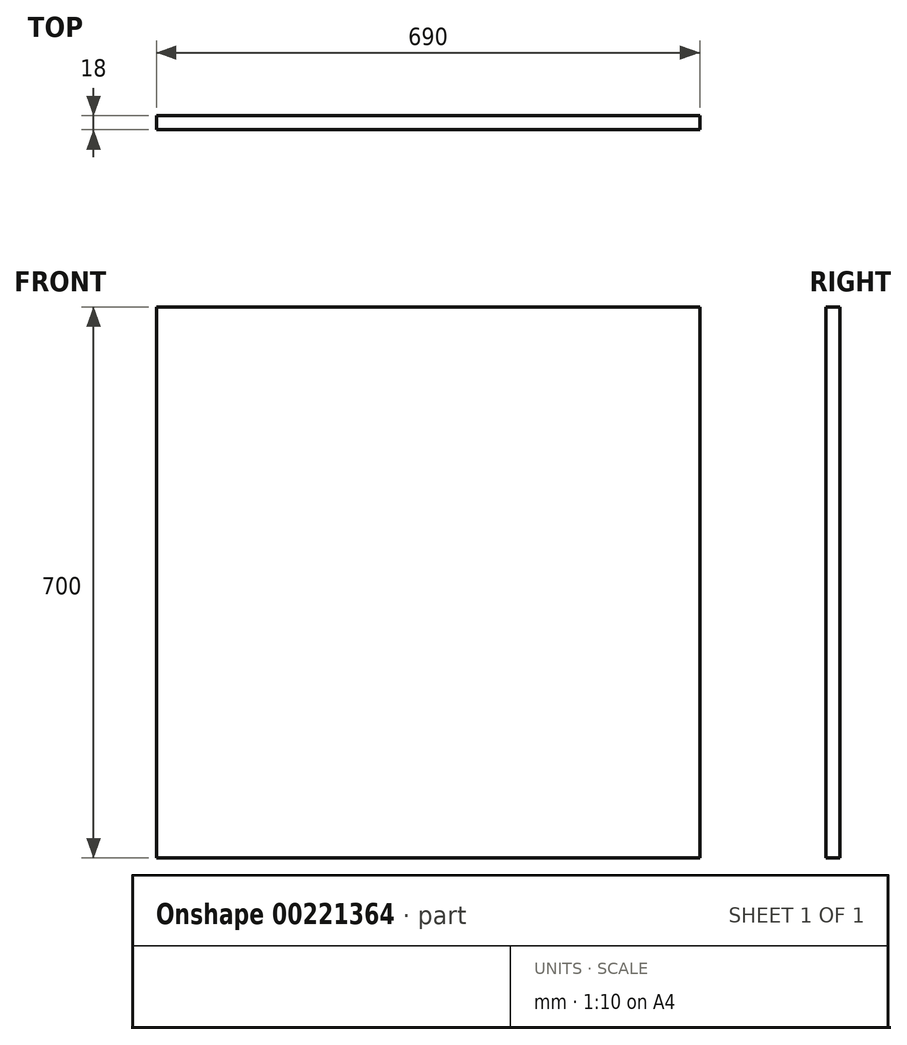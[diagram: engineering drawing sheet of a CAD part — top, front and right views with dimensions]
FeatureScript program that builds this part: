
annotation { "Feature Type Name" : "Feature", "Feature Type Description" : "" }
export const myFeature = defineFeature(function(context is Context, id is Id, definition is map)
    precondition{}
    {
        {
            var Q0;
            Q0=qCreatedBy(makeId("Front.planeOp"),FACE);
            var sketch = newSketch(context, id + "F0", { "sketchPlane" : qUnion([Q0])});
            skLineSegment(sketch, "E0.bottom", {"start": v(345, -350) * mm, "end": v(-345, -350) * mm});
            skLineSegment(sketch, "E0.top", {"start": v(345, 350) * mm, "end": v(-345, 350) * mm});
            skLineSegment(sketch, "E0.left", {"start": v(345, -350) * mm, "end": v(345, 350) * mm});
            skLineSegment(sketch, "E0.right", {"start": v(-345, -350) * mm, "end": v(-345, 350) * mm});
            skPoint(sketch, "E0.middle", {"position": v(0, 0) * mm});
            skSolve(sketch);
        }
        {
            var Q0;
            Q0 = qSketchRegion(id + "F0", true);
            extrude(context, id + "F1", {"entities" : qUnion([Q0]), "depth" : 18 * mm});
        }
    });
